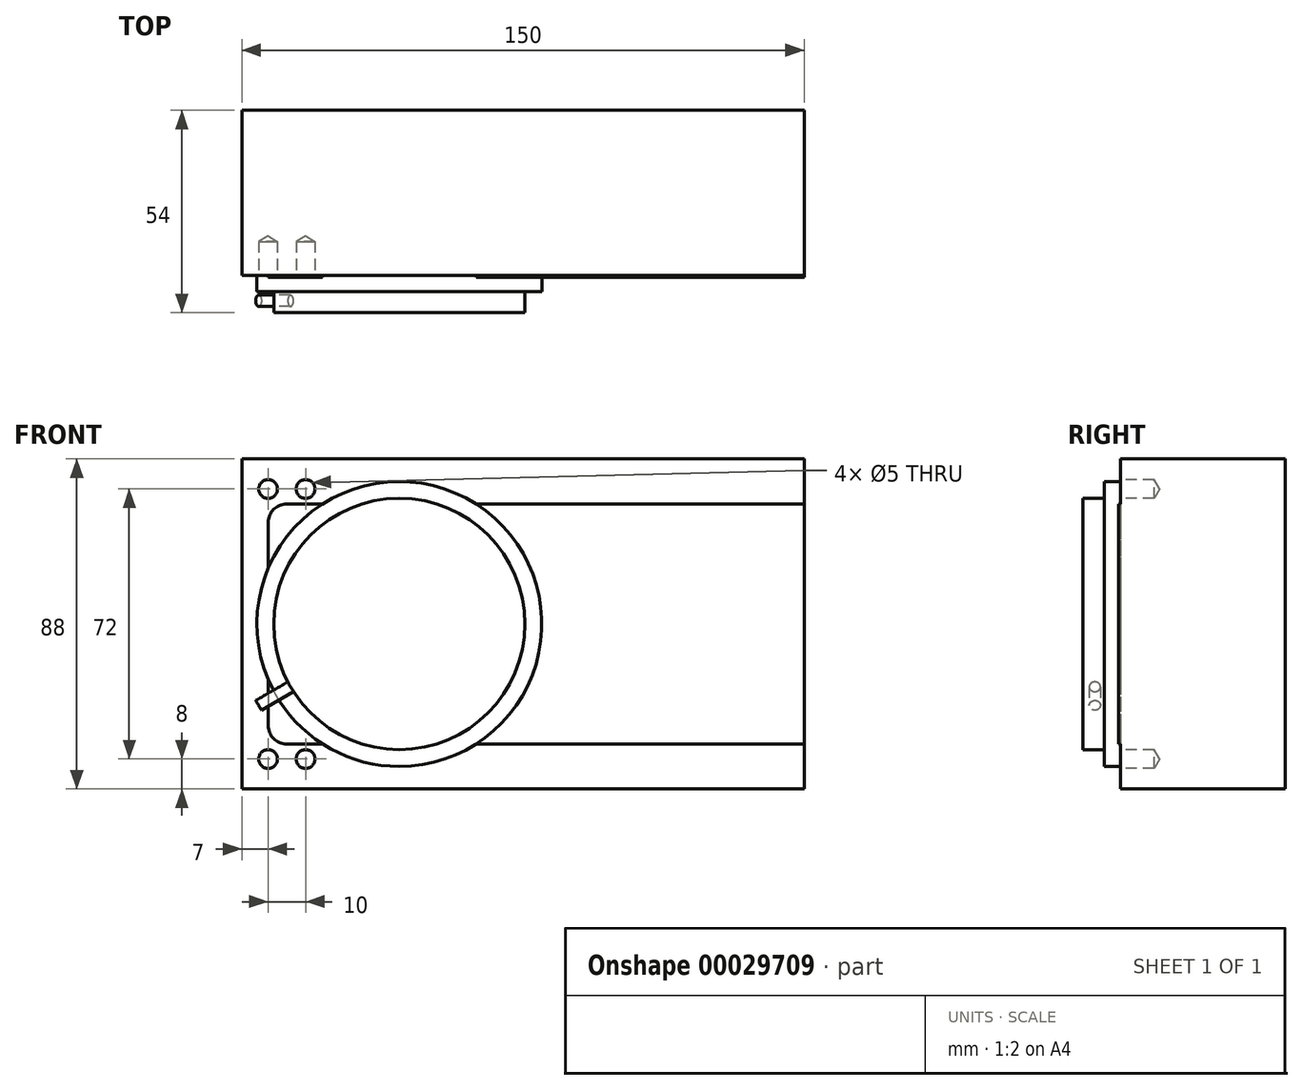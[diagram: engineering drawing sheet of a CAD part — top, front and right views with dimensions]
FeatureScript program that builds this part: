
annotation { "Feature Type Name" : "Feature", "Feature Type Description" : "" }
export const myFeature = defineFeature(function(context is Context, id is Id, definition is map)
    precondition{}
    {
        {
            var Q0;
            Q0=qCreatedBy(makeId("Front.planeOp"),FACE);
            var sketch = newSketch(context, id + "F0", { "sketchPlane" : qUnion([Q0])});
            skLineSegment(sketch, "E0.bottom", {"start": v(-42, 44) * mm, "end": v(108, 44) * mm});
            skLineSegment(sketch, "E0.top", {"start": v(-42, -44) * mm, "end": v(108, -44) * mm});
            skLineSegment(sketch, "E0.left", {"start": v(-42, 44) * mm, "end": v(-42, -44) * mm});
            skLineSegment(sketch, "E0.right", {"start": v(108, 44) * mm, "end": v(108, -44) * mm});
            skSolve(sketch);
        }
        {
            var Q0;
            Q0 = qSketchRegion(id + "F0", true);
            extrude(context, id + "F1", {"entities" : qUnion([Q0]), "oppositeDirection" : true, "depth" : 44 * mm});
        }
        {
            var Q0;
            Q0=makeQuery(id+"F1.opExtrude","CAP_FACE",FACE,{"disambiguationData":[OSD([sQuery(id+"F0.wireOp",EDGE,"E0.bottom"),sQuery(id+"F0.wireOp",EDGE,"E0.top"),sQuery(id+"F0.wireOp",EDGE,"E0.left"),sQuery(id+"F0.wireOp",EDGE,"E0.right")])],"isStart":true});
            var sketch = newSketch(context, id + "F2", { "sketchPlane" : qUnion([Q0])});
            skLineSegment(sketch, "E1.bottom", {"start": v(-30, 32) * mm, "end": v(108, 32) * mm});
            skLineSegment(sketch, "E1.top", {"start": v(-30, -32) * mm, "end": v(108, -32) * mm});
            skLineSegment(sketch, "E1.left", {"start": v(-35, 27) * mm, "end": v(-35, -27) * mm});
            skLineSegment(sketch, "E1.right", {"start": v(108, 32) * mm, "end": v(108, -32) * mm});
            skPoint(sketch, "E2.visualSharp", {"position": v(-35, 32) * mm});
            skArc(sketch, "E2.filletArc", {"start": v(-30, 32) * mm, "mid": v(-33.54, 30.54) * mm, "end": v(-35, 27) * mm});
            skPoint(sketch, "E3.visualSharp", {"position": v(-35, -32) * mm});
            skArc(sketch, "E3.filletArc", {"start": v(-35, -27) * mm, "mid": v(-33.54, -30.54) * mm, "end": v(-30, -32) * mm});
            skSolve(sketch);
        }
        {
            var Q0;
            Q0 = qSketchRegion(id + "F2", true);
            var Q1;
            Q1=makeQuery(id+"F2.imprint","IMPRINT",FACE,{"disambiguationData":[TD([[makeQuery(id+"F2.imprint","IMPRINT",EDGE,{"derivedFrom":sQuery(id+"F2.wireOp",EDGE,"E1.bottom")}),-1.0]])]});
            extrude(context, id + "F3", {"entities" : qUnion([Q0, Q1]), "operationType" : NewBodyOperationType.ADD, "depth" : 0.5 * mm});
        }
        {
            var Q0;
            Q0=makeQuery(id+"F1.opExtrude","CAP_FACE",FACE,{"disambiguationData":[OSD([sQuery(id+"F0.wireOp",EDGE,"E0.bottom"),sQuery(id+"F0.wireOp",EDGE,"E0.top"),sQuery(id+"F0.wireOp",EDGE,"E0.left"),sQuery(id+"F0.wireOp",EDGE,"E0.right")])],"isStart":true});
            var sketch = newSketch(context, id + "F4", { "sketchPlane" : qUnion([Q0])});
            skPoint(sketch, "E4", {"position": v(-35, 36) * mm});
            skPoint(sketch, "E5", {"position": v(-25, 36) * mm});
            skPoint(sketch, "E6", {"position": v(-35, -36) * mm});
            skPoint(sketch, "E7", {"position": v(-25, -36) * mm});
            skSolve(sketch);
        }
        {
            var Q0;
            Q0=sQuery(id+"F4.wireOp",VERTEX,"E4");
            var Q1;
            Q1=sQuery(id+"F4.wireOp",VERTEX,"E5");
            var Q2;
            Q2=sQuery(id+"F4.wireOp",VERTEX,"E6");
            var Q3;
            Q3=sQuery(id+"F4.wireOp",VERTEX,"E7");
            var Q4;
            Q4=makeQuery(id+"F1.opExtrude","SWEPT_BODY",BODY,{"disambiguationData":[OSD([sQuery(id+"F0.wireOp",EDGE,"E0.bottom"),sQuery(id+"F0.wireOp",EDGE,"E0.top"),sQuery(id+"F0.wireOp",EDGE,"E0.left"),sQuery(id+"F0.wireOp",EDGE,"E0.right")])]});
            hole(context, id + "F5", {"style" : HoleStyle.SIMPLE, "holeDiameter" : 5 * mm, "endStyle" : HoleEndStyle.BLIND, "holeDepth" : 9 * mm, "locations" : qUnion([Q0, Q1, Q2, Q3]), "scope" : qUnion([Q4])});
        }
        {
            var Q0;
            Q0=qCreatedBy(makeId("Front.planeOp"),FACE);
            var sketch = newSketch(context, id + "F6", { "sketchPlane" : qUnion([Q0])});
            skCircle(sketch, "E8", {"center": v(0, 0) * mm, "radius": 33.5 * mm});
            skSolve(sketch);
        }
        {
            var Q0;
            Q0=makeQuery(id+"F6.imprint","IMPRINT",FACE,{"disambiguationData":[TD([[makeQuery(id+"F6.imprint","IMPRINT",EDGE,{"derivedFrom":sQuery(id+"F6.wireOp",EDGE,"E8")}),1.0]])]});
            extrude(context, id + "F7", {"entities" : qUnion([Q0]), "operationType" : NewBodyOperationType.ADD, "depth" : 10 * mm});
        }
        {
            var Q0;
            {var subQ0=sQuery(id+"F2.wireOp",EDGE,"E1.top");var subQ1=sQuery(id+"F2.wireOp",EDGE,"E1.left");var subQ2=sQuery(id+"F2.wireOp",EDGE,"E3.filletArc");Q0=makeQuery(id+"F7.boolean.opBoolean","SPLIT",FACE,{"disambiguationData":[TD([makeQuery(id+"F3.opExtrude","SWEPT_FACE",FACE,{"disambiguationData":[OSD([subQ2])]})])],"derivedFrom":makeQuery(id+"F3.opExtrude","CAP_FACE",FACE,{"disambiguationData":[OSD([sQuery(id+"F2.wireOp",EDGE,"E1.bottom"),subQ0,subQ1,sQuery(id+"F2.wireOp",EDGE,"E1.right"),sQuery(id+"F2.wireOp",EDGE,"E2.filletArc"),subQ2])],"isStart":false})});}
            cPlane(context, id + "F8", {"entities" : qUnion([Q0]), "cplaneType" : CPlaneType.OFFSET, "offset" : 6.3 * mm, "width" : 150 * mm, "height" : 150 * mm});
        }
        {
            var Q0;
            Q0=qCreatedBy(id+"F8.planeOp",FACE);
            var sketch = newSketch(context, id + "F9", { "sketchPlane" : qUnion([Q0])});
            skLineSegment(sketch, "E9", {"start": v(0, 0) * mm, "end": v(-33.37, -19.27) * mm, "construction": true});
            skLineSegment(sketch, "E10", {"start": v(-38.3, -20.38) * mm, "end": v(-11.88, -5.13) * mm});
            skLineSegment(sketch, "E11", {"start": v(-11.88, -5.13) * mm, "end": v(-10.38, -7.73) * mm});
            skLineSegment(sketch, "E12", {"start": v(-10.38, -7.73) * mm, "end": v(-36.8, -22.97) * mm});
            skLineSegment(sketch, "E13", {"start": v(-36.8, -22.97) * mm, "end": v(-38.3, -20.38) * mm});
            skCircle(sketch, "E14.0", {"center": v(0, 0) * mm, "radius": 33.5 * mm});
            skSolve(sketch);
        }
        {
            var Q0;
            {var subQ5=sQuery(id+"F9.wireOp",EDGE,"E13");Q0=makeQuery(id+"F9.imprint","IMPRINT",FACE,{"disambiguationData":[TD([[makeQuery(id+"F9.imprint","IMPRINT",EDGE,{"derivedFrom":subQ5}),-1.0]])]});}
            extrude(context, id + "F10", {"entities" : qUnion([Q0]), "operationType" : NewBodyOperationType.ADD, "endBound" : BoundingType.SYMMETRIC, "depth" : 3 * mm});
        }
        {
            var Q0;
            Q0=makeQuery(id+"F10.opExtrude","CAP_EDGE",EDGE,{"disambiguationData":[OSD([sQuery(id+"F9.wireOp",EDGE,"E10")])],"isStart":false});
            var Q1;
            Q1=makeQuery(id+"F10.opExtrude","CAP_EDGE",EDGE,{"disambiguationData":[OSD([sQuery(id+"F9.wireOp",EDGE,"E12")])],"isStart":false});
            var Q2;
            Q2=makeQuery(id+"F10.opExtrude","CAP_EDGE",EDGE,{"disambiguationData":[OSD([sQuery(id+"F9.wireOp",EDGE,"E12")])],"isStart":true});
            var Q3;
            Q3=makeQuery(id+"F10.opExtrude","CAP_EDGE",EDGE,{"disambiguationData":[OSD([sQuery(id+"F9.wireOp",EDGE,"E10")])],"isStart":true});
            fillet(context, id + "F11", {"entities" : qUnion([Q0, Q1, Q2, Q3]), "radius" : 1.5 * mm, "allowEdgeOverflow" : false});
        }
        {
            var Q0;
            Q0=qCreatedBy(makeId("Front.planeOp"),FACE);
            var sketch = newSketch(context, id + "F12", { "sketchPlane" : qUnion([Q0])});
            skCircle(sketch, "E15", {"center": v(0, 0) * mm, "radius": 38 * mm});
            skSolve(sketch);
        }
        {
            var Q0;
            Q0 = qSketchRegion(id + "F12", true);
            var Q1;
            Q1=makeQuery(id+"F12.imprint","IMPRINT",FACE,{"disambiguationData":[TD([[makeQuery(id+"F12.imprint","IMPRINT",EDGE,{"derivedFrom":sQuery(id+"F12.wireOp",EDGE,"E15")}),1.0]])]});
            extrude(context, id + "F13", {"entities" : qUnion([Q0, Q1]), "operationType" : NewBodyOperationType.ADD, "depth" : 4.3 * mm});
        }
    });
